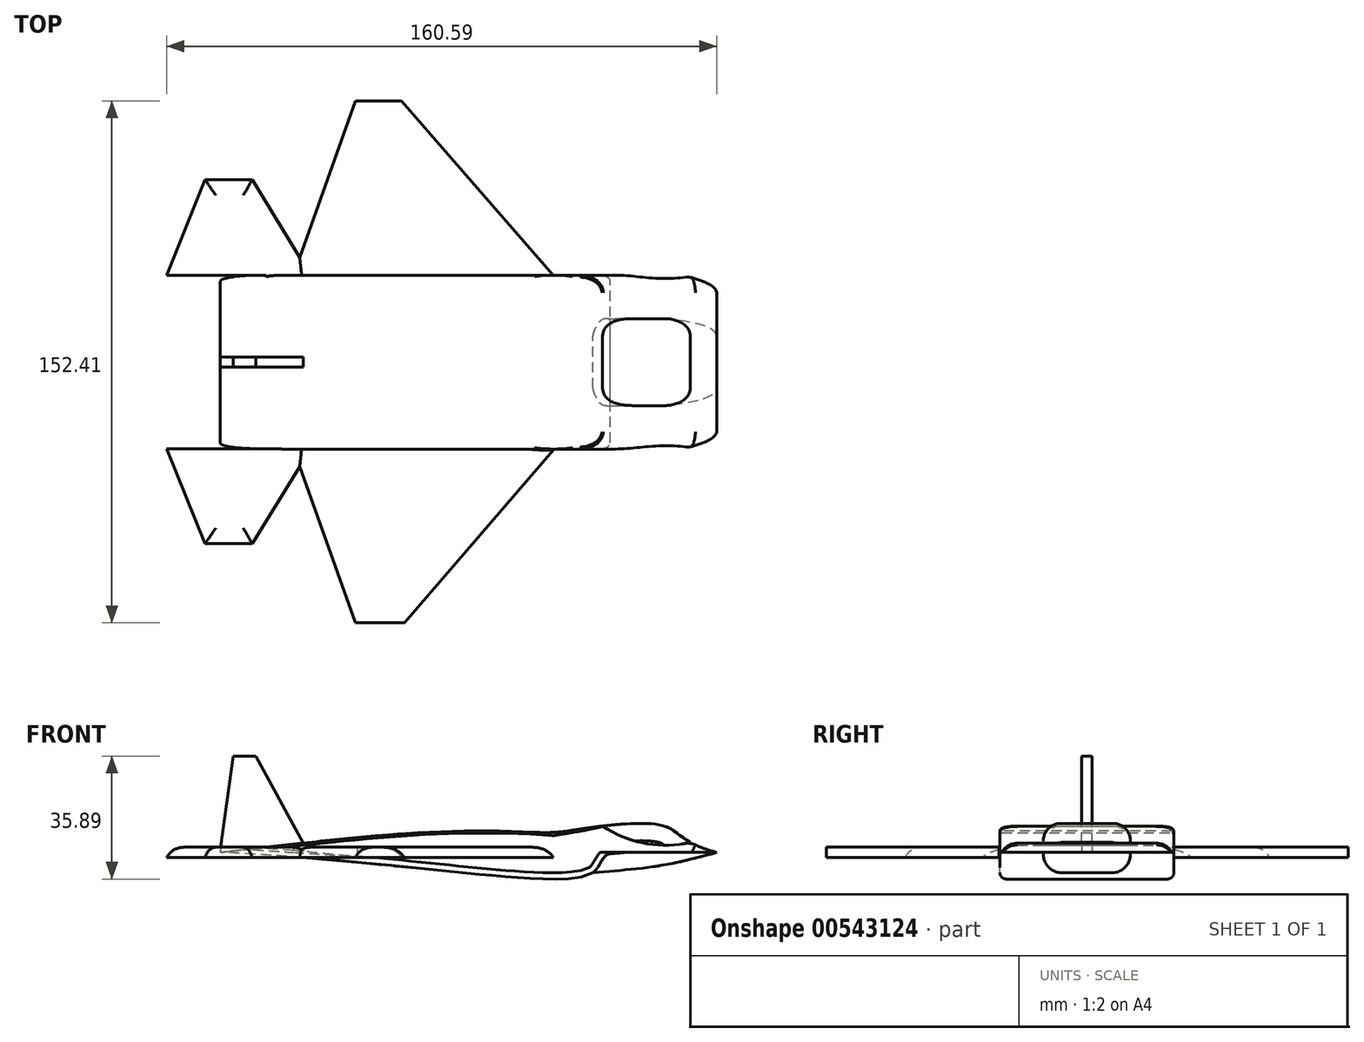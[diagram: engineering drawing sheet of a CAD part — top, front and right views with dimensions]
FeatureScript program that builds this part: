
annotation { "Feature Type Name" : "Feature", "Feature Type Description" : "" }
export const myFeature = defineFeature(function(context is Context, id is Id, definition is map)
    precondition{}
    {
        {
            var Q0;
            Q0=qCreatedBy(makeId("Front.planeOp"),FACE);
            var sketch = newSketch(context, id + "F0", { "sketchPlane" : qUnion([Q0])});
            skLineSegment(sketch, "E0", {"start": v(-76.12, 0) * mm, "end": v(76.48, 0) * mm});
            skFitSpline(sketch, "E1", {"points": [v(-68.54, 0) * mm, v(40.33, -5.9) * mm, v(45.44, 0) * mm], "startDerivative": vector(212.09, -9.68) * mm, "endDerivative": vector(45.28, 24.96) * mm});
            skFitSpline(sketch, "E2", {"points": [v(40.33, -5.9) * mm, v(76.48, 0) * mm], "startDerivative": vector(54.25, 4.45) * mm, "endDerivative": vector(44.52, 12.21) * mm});
            skFitSpline(sketch, "E3", {"points": [v(76.48, 0) * mm, v(61, 7.79) * mm, v(28.85, 5.49) * mm], "startDerivative": vector(-77.5, 20.8) * mm, "endDerivative": vector(-54.3, -10.13) * mm});
            skArc(sketch, "E4", {"start": v(43.18, 7.7) * mm, "mid": v(55.5, 2.64) * mm, "end": v(68.81, 2.93) * mm});
            skFitSpline(sketch, "E5", {"points": [v(28.85, 5.49) * mm, v(-68.54, 0) * mm], "startDerivative": vector(-96.65, 7.97) * mm, "endDerivative": vector(-102.6, -11.15) * mm});
            skSolve(sketch);
        }
        {
            var Q0;
            Q0=qCreatedBy(makeId("Top.planeOp"),FACE);
            var sketch = newSketch(context, id + "F1", { "sketchPlane" : qUnion([Q0])});
            skLineSegment(sketch, "E6", {"start": v(28.82, 25.31) * mm, "end": v(-15.5, 76.3) * mm});
            skLineSegment(sketch, "E7", {"start": v(-15.5, 76.3) * mm, "end": v(-29.07, 76.3) * mm});
            skLineSegment(sketch, "E8", {"start": v(-29.07, 76.3) * mm, "end": v(-47.12, 25.4) * mm});
            skLineSegment(sketch, "E9", {"start": v(-14.73, -76.12) * mm, "end": v(-29.07, -76.12) * mm});
            skLineSegment(sketch, "E10", {"start": v(-47.12, -25.31) * mm, "end": v(-29.07, -76.12) * mm});
            skLineSegment(sketch, "E11", {"start": v(-14.73, -76.12) * mm, "end": v(28.82, -25.67) * mm});
            skLineSegment(sketch, "E12", {"start": v(-45.28, 30.6) * mm, "end": v(-59.18, 53.3) * mm});
            skLineSegment(sketch, "E13", {"start": v(-59.18, 53.3) * mm, "end": v(-72.94, 53.3) * mm});
            skLineSegment(sketch, "E14", {"start": v(-72.94, 53.3) * mm, "end": v(-84.1, 25.4) * mm});
            skLineSegment(sketch, "E15", {"start": v(-84.1, -25.31) * mm, "end": v(-68.43, -25.31) * mm});
            skLineSegment(sketch, "E16", {"start": v(-84.1, 25.4) * mm, "end": v(-68.46, 25.4) * mm});
            skLineSegment(sketch, "E17", {"start": v(-45.28, -30.5) * mm, "end": v(-59.18, -53.08) * mm});
            skLineSegment(sketch, "E18", {"start": v(-72.94, -53.08) * mm, "end": v(-84.1, -25.31) * mm});
            skLineSegment(sketch, "E19", {"start": v(-72.94, -53.08) * mm, "end": v(-59.18, -53.08) * mm});
            skLineSegment(sketch, "E20", {"start": v(-47.12, 25.4) * mm, "end": v(-68.46, 25.4) * mm});
            skLineSegment(sketch, "E21", {"start": v(28.82, 25.31) * mm, "end": v(-47.12, 25.4) * mm});
            skLineSegment(sketch, "E22", {"start": v(-68.43, -25.31) * mm, "end": v(-47.12, -25.31) * mm});
            skLineSegment(sketch, "E23", {"start": v(-47.12, -25.31) * mm, "end": v(28.82, -25.67) * mm});
            skSolve(sketch);
        }
        {
            var Q0;
            {var subQ0=sQuery(id+"F0.wireOp",EDGE,"E1");var subQ1=sQuery(id+"F0.wireOp",EDGE,"E0");var subQ3=makeQuery(id+"F0.imprint","INTERSECT",VERTEX,{"derivedFrom":[subQ1,subQ0]});Q0=makeQuery(id+"F0.imprint","IMPRINT",FACE,{"disambiguationData":[TD([[makeQuery(id+"F0.imprint","IMPRINT",EDGE,{"disambiguationData":[TD([[subQ3,1.0]])],"derivedFrom":subQ0}),1.0]])]});}
            var Q1;
            {var subQ2=sQuery(id+"F0.wireOp",EDGE,"E4");Q1=makeQuery(id+"F0.imprint","IMPRINT",FACE,{"disambiguationData":[TD([[makeQuery(id+"F0.imprint","IMPRINT",EDGE,{"derivedFrom":subQ2}),-1.0]])]});}
            extrude(context, id + "F2", {"entities" : qUnion([Q0, Q1]), "endBound" : BoundingType.SYMMETRIC, "depth" : 50.8 * mm, "offsetDistance" : 25.4 * mm});
        }
        {
            var Q0;
            {var subQ0=sQuery(id+"F0.wireOp",EDGE,"E2");Q0=makeQuery(id+"F0.imprint","IMPRINT",FACE,{"disambiguationData":[TD([[makeQuery(id+"F0.imprint","IMPRINT",EDGE,{"derivedFrom":subQ0}),1.0]])]});}
            var Q1;
            {var subQ0=sQuery(id+"F0.wireOp",EDGE,"E4");Q1=makeQuery(id+"F0.imprint","IMPRINT",FACE,{"disambiguationData":[TD([[makeQuery(id+"F0.imprint","IMPRINT",EDGE,{"derivedFrom":subQ0}),1.0]])]});}
            extrude(context, id + "F3", {"entities" : qUnion([Q0, Q1]), "endBound" : BoundingType.SYMMETRIC, "depth" : 25.4 * mm, "offsetDistance" : 25.4 * mm});
        }
        {
            var Q0;
            Q0 = qSketchRegion(id + "F1", true);
            extrude(context, id + "F4", {"entities" : qUnion([Q0]), "operationType" : NewBodyOperationType.ADD, "endBound" : BoundingType.SYMMETRIC, "depth" : 3 * mm, "offsetDistance" : 25.4 * mm});
        }
        {
            var Q0;
            {var subQ0=sQuery(id+"F0.wireOp",EDGE,"E3");Q0=makeQuery(id+"F2.opExtrude","CAP_EDGE",EDGE,{"disambiguationData":[OSD([subQ0]),TDD([makeQuery(id+"F0.imprint","IMPRINT",EDGE,{"disambiguationData":[TD([[makeQuery(id+"F0.imprint","INTERSECT",VERTEX,{"disambiguationData":[OD(1.0)],"derivedFrom":[subQ0,sQuery(id+"F0.wireOp",EDGE,"E4")]}),1.0]])],"derivedFrom":subQ0})])],"isStart":true});}
            var Q1;
            {var subQ0=sQuery(id+"F0.wireOp",EDGE,"E3");Q1=makeQuery(id+"F2.opExtrude","CAP_EDGE",EDGE,{"disambiguationData":[OSD([subQ0]),TDD([makeQuery(id+"F0.imprint","IMPRINT",EDGE,{"disambiguationData":[TD([[makeQuery(id+"F0.imprint","INTERSECT",VERTEX,{"disambiguationData":[OD(1.0)],"derivedFrom":[subQ0,sQuery(id+"F0.wireOp",EDGE,"E4")]}),1.0]])],"derivedFrom":subQ0})])],"isStart":false});}
            fillet(context, id + "F5", {"entities" : qUnion([Q0, Q1]), "radius" : 5.08 * mm, "tangentPropagation" : true, "allowEdgeOverflow" : false});
        }
        {
            var Q0;
            Q0=makeQuery(id+"F2.opExtrude","CAP_EDGE",EDGE,{"disambiguationData":[OSD([sQuery(id+"F0.wireOp",EDGE,"E4")])],"isStart":false});
            var Q1;
            Q1=makeQuery(id+"F3.opExtrude","CAP_EDGE",EDGE,{"disambiguationData":[OSD([sQuery(id+"F0.wireOp",EDGE,"E3")])],"isStart":false});
            var Q2;
            Q2=makeQuery(id+"F3.opExtrude","CAP_EDGE",EDGE,{"disambiguationData":[OSD([sQuery(id+"F0.wireOp",EDGE,"E3")])],"isStart":true});
            fillet(context, id + "F6", {"entities" : qUnion([Q0, Q1, Q2]), "radius" : 5.08 * mm, "tangentPropagation" : true, "allowEdgeOverflow" : false});
        }
        {
            var Q0;
            Q0=makeQuery(id+"F2.opExtrude","CAP_EDGE",EDGE,{"disambiguationData":[OSD([sQuery(id+"F0.wireOp",EDGE,"E1")])],"isStart":false});
            var Q1;
            {var subQ0=sQuery(id+"F0.wireOp",EDGE,"E1");Q1=makeQuery(id+"F4.boolean.opBoolean","SPLIT",EDGE,{"disambiguationData":[topologyDisambiguationEdgeConnected([makeQuery(id+"F2.opExtrude","CAP_FACE",FACE,{"disambiguationData":[OSD([sQuery(id+"F0.wireOp",EDGE,"E0"),subQ0,sQuery(id+"F0.wireOp",EDGE,"E3"),sQuery(id+"F0.wireOp",EDGE,"E4"),sQuery(id+"F0.wireOp",EDGE,"E5")])],"isStart":true})])],"derivedFrom":makeQuery(id+"F2.opExtrude","CAP_EDGE",EDGE,{"disambiguationData":[OSD([subQ0])],"isStart":true})});}
            fillet(context, id + "F7", {"entities" : qUnion([Q0, Q1]), "radius" : 1.84 * mm, "tangentPropagation" : true, "allowEdgeOverflow" : false});
        }
        {
            var Q0;
            {var subQ0=sQuery(id+"F0.wireOp",EDGE,"E5");Q0=makeQuery(id+"F4.boolean.opBoolean","SPLIT",EDGE,{"disambiguationData":[topologyDisambiguationEdgeConnected([makeQuery(id+"F2.opExtrude","CAP_FACE",FACE,{"disambiguationData":[OSD([sQuery(id+"F0.wireOp",EDGE,"E0"),sQuery(id+"F0.wireOp",EDGE,"E1"),sQuery(id+"F0.wireOp",EDGE,"E3"),sQuery(id+"F0.wireOp",EDGE,"E4"),subQ0])],"isStart":true})])],"derivedFrom":makeQuery(id+"F2.opExtrude","CAP_EDGE",EDGE,{"disambiguationData":[OSD([subQ0])],"isStart":true})});}
            var Q1;
            {var subQ0=sQuery(id+"F0.wireOp",EDGE,"E3");Q1=makeQuery(id+"F2.opExtrude","CAP_EDGE",EDGE,{"disambiguationData":[OSD([subQ0]),TDD([makeQuery(id+"F0.imprint","IMPRINT",EDGE,{"disambiguationData":[TD([[makeQuery(id+"F0.imprint","INTERSECT",VERTEX,{"derivedFrom":[subQ0,sQuery(id+"F0.wireOp",EDGE,"E5")]}),1.0]])],"derivedFrom":subQ0})])],"isStart":true});}
            var Q2;
            Q2=makeQuery(id+"F2.opExtrude","CAP_EDGE",EDGE,{"disambiguationData":[OSD([sQuery(id+"F0.wireOp",EDGE,"E5")])],"isStart":false});
            var Q3;
            {var subQ0=sQuery(id+"F0.wireOp",EDGE,"E3");Q3=makeQuery(id+"F2.opExtrude","CAP_EDGE",EDGE,{"disambiguationData":[OSD([subQ0]),TDD([makeQuery(id+"F0.imprint","IMPRINT",EDGE,{"disambiguationData":[TD([[makeQuery(id+"F0.imprint","INTERSECT",VERTEX,{"derivedFrom":[subQ0,sQuery(id+"F0.wireOp",EDGE,"E5")]}),1.0]])],"derivedFrom":subQ0})])],"isStart":false});}
            fillet(context, id + "F8", {"entities" : qUnion([Q0, Q1, Q2, Q3]), "radius" : 0.61 * mm, "tangentPropagation" : true, "allowEdgeOverflow" : false});
        }
        {
            var Q0;
            Q0=makeQuery(id+"F4.opExtrude","CAP_EDGE",EDGE,{"disambiguationData":[OSD([sQuery(id+"F1.wireOp",EDGE,"E13")])],"isStart":false});
            var Q1;
            Q1=makeQuery(id+"F4.opExtrude","CAP_EDGE",EDGE,{"disambiguationData":[OSD([sQuery(id+"F1.wireOp",EDGE,"E14")])],"isStart":false});
            var Q2;
            Q2=makeQuery(id+"F4.opExtrude","CAP_EDGE",EDGE,{"disambiguationData":[OSD([sQuery(id+"F1.wireOp",EDGE,"E12")])],"isStart":false});
            var Q3;
            Q3=makeQuery(id+"F4.opExtrude","CAP_EDGE",EDGE,{"disambiguationData":[OSD([sQuery(id+"F1.wireOp",EDGE,"E8")])],"isStart":false});
            var Q4;
            Q4=makeQuery(id+"F4.opExtrude","CAP_EDGE",EDGE,{"disambiguationData":[OSD([sQuery(id+"F1.wireOp",EDGE,"E6")])],"isStart":false});
            fillet(context, id + "F9", {"entities" : qUnion([Q0, Q1, Q2, Q3, Q4]), "radius" : 5.08 * mm, "tangentPropagation" : true, "allowEdgeOverflow" : false});
        }
        {
            var Q0;
            Q0=makeQuery(id+"F4.opExtrude","CAP_EDGE",EDGE,{"disambiguationData":[OSD([sQuery(id+"F1.wireOp",EDGE,"E11")])],"isStart":false});
            var Q1;
            Q1=makeQuery(id+"F4.opExtrude","CAP_EDGE",EDGE,{"disambiguationData":[OSD([sQuery(id+"F1.wireOp",EDGE,"E10")])],"isStart":false});
            var Q2;
            Q2=makeQuery(id+"F4.opExtrude","CAP_EDGE",EDGE,{"disambiguationData":[OSD([sQuery(id+"F1.wireOp",EDGE,"E17")])],"isStart":false});
            var Q3;
            Q3=makeQuery(id+"F4.opExtrude","CAP_EDGE",EDGE,{"disambiguationData":[OSD([sQuery(id+"F1.wireOp",EDGE,"E19")])],"isStart":false});
            var Q4;
            Q4=makeQuery(id+"F4.opExtrude","CAP_EDGE",EDGE,{"disambiguationData":[OSD([sQuery(id+"F1.wireOp",EDGE,"E18")])],"isStart":false});
            fillet(context, id + "F10", {"entities" : qUnion([Q0, Q1, Q2, Q3, Q4]), "radius" : 5.08 * mm, "tangentPropagation" : true, "allowEdgeOverflow" : false});
        }
        {
            var Q0;
            Q0=makeQuery(id+"F3.opExtrude","CAP_EDGE",EDGE,{"disambiguationData":[OSD([sQuery(id+"F0.wireOp",EDGE,"E2")])],"isStart":false});
            var Q1;
            Q1=makeQuery(id+"F3.opExtrude","CAP_EDGE",EDGE,{"disambiguationData":[OSD([sQuery(id+"F0.wireOp",EDGE,"E2")])],"isStart":true});
            fillet(context, id + "F11", {"entities" : qUnion([Q0, Q1]), "radius" : 5.08 * mm, "tangentPropagation" : true, "allowEdgeOverflow" : false});
        }
        {
            var Q0;
            Q0=qCreatedBy(makeId("Front.planeOp"),FACE);
            var sketch = newSketch(context, id + "F12", { "sketchPlane" : qUnion([Q0])});
            skLineSegment(sketch, "E24", {"start": v(-68.55, 0) * mm, "end": v(-42.82, 0) * mm});
            skLineSegment(sketch, "E25", {"start": v(-42.82, 0) * mm, "end": v(-58.14, 28.1) * mm});
            skLineSegment(sketch, "E26", {"start": v(-58.14, 28.1) * mm, "end": v(-64.76, 28.1) * mm});
            skLineSegment(sketch, "E27", {"start": v(-64.76, 28.1) * mm, "end": v(-68.55, 0) * mm});
            skSolve(sketch);
        }
        {
            var Q0;
            Q0 = qSketchRegion(id + "F12", true);
            extrude(context, id + "F13", {"entities" : qUnion([Q0]), "operationType" : NewBodyOperationType.ADD, "endBound" : BoundingType.SYMMETRIC, "depth" : 3 * mm, "offsetDistance" : 25.4 * mm});
        }
        {
            var Q0;
            Q0=makeQuery(id+"F2.opExtrude","SWEPT_EDGE",EDGE,{"disambiguationData":[OSD([sQuery(id+"F0.wireOp",EDGE,"E3"),sQuery(id+"F0.wireOp",EDGE,"E5")])]});
            fillet(context, id + "F14", {"entities" : qUnion([Q0]), "radius" : 50.8 * mm, "tangentPropagation" : true, "allowEdgeOverflow" : false});
        }
    });
